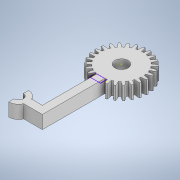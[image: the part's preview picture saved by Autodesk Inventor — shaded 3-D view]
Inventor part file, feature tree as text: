
AUTODESK INVENTOR PART (.ipt)
format: ipt  version: 2022 (Build 260153000, 153)  size: 308,736 bytes
history: native  units: in
note: dims shown in document units (in); Inventor stores cm internally (conversion verified against a paired STEP export)
features: sketch x8, extrude x7, pattern_circular x1
ambient origin geometry x8: Origin, YZ Plane, XZ Plane, XY Plane, X Axis, Y Axis, Z Axis, Center Point
bodies: Solid1 (feature_tree)
feature tree (16):
  extrude  "Extrusion1"  Depth=0.1575in
  pattern_circular  "Circular Pattern1"  Count=26 Angle=360.0deg
  extrude  "Extrusion6"  Depth=0.1969in
  extrude  "Extrusion9"  Depth=0.1969in
  extrude  "Extrusion10"  Depth=0.1969in TaperAngle=0.0deg
  sketch  "Sketch13"  dims[d7=0.0472in]
  extrude  "Extrusion11"  Depth=0.1969in
  extrude  "Extrusion12"  Depth=0.1969in
  extrude  "Extrusion13"  Depth=0.1969in
  sketch  "Sketch1"  dims[d0=0.6299in d1=0.1575in]
  sketch  "Sketch8"  dims[d2=0.0098in]
  sketch  "Sketch11"  dims[d3=0.0098in]
  sketch  "Sketch12"  dims[d4=0.0236in]
  sketch  "Sketch14"  dims[d8=0.1772in]
  sketch  "Sketch15"  dims[d10=0.0787in]
  sketch  "Sketch16"  dims[d11=0.1969in d12=0.0in d13=10.2362in d14=360.0deg d49=0.1969in d50=0.1575in d51=0.5438in d52=0.0in d84=1.1811in d85=0.3543in d86=0.1378in d87=0.3937in d88=0.0in d89=0.0591in d90=0.0591in d91=0.3937in d92=0.0in d93=0.3937in d94=0.0in d95=0.3543in d96=1.1811in d97=0.1181in d98=0.0591in d99=0.0591in d100=0.1378in d101=0.1969in d102=0.1969in d103=0.0in d104=0.0787in d105=0.0787in d106=0.2953in d107=0.1969in d108=0.1969in d109=0.0in d69=0.0197in d70=0.0344in d71=0.0197in d72=0.0344in]
